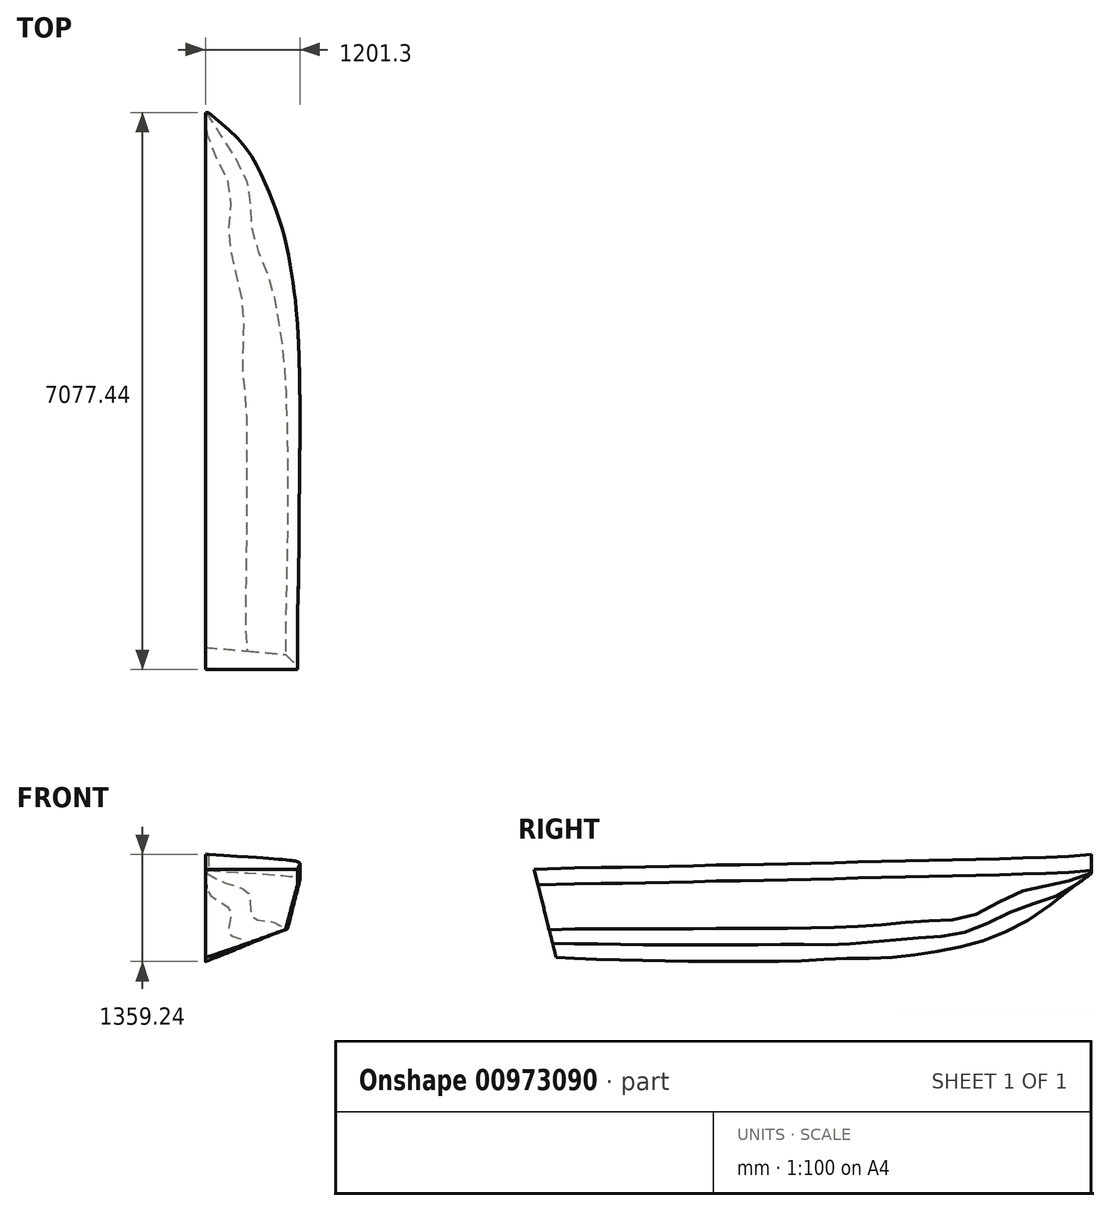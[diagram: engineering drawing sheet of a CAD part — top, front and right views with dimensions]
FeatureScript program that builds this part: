
annotation { "Feature Type Name" : "Feature", "Feature Type Description" : "" }
export const myFeature = defineFeature(function(context is Context, id is Id, definition is map)
    precondition{}
    {
        {
            var Q0;
            Q0=qCreatedBy(makeId("Front.planeOp"),FACE);
            cPlane(context, id + "F0", {"entities" : qUnion([Q0]), "cplaneType" : CPlaneType.OFFSET, "offset" : 946.15 * mm, "width" : 152.4 * mm, "height" : 152.4 * mm});
        }
        {
            var Q0;
            Q0=qCreatedBy(makeId("Front.planeOp"),FACE);
            cPlane(context, id + "F1", {"entities" : qUnion([Q0]), "cplaneType" : CPlaneType.OFFSET, "offset" : 1504.95 * mm, "width" : 152.4 * mm, "height" : 152.4 * mm});
        }
        {
            var Q0;
            Q0=qCreatedBy(id+"F0.planeOp",FACE);
            var sketch = newSketch(context, id + "F2", { "sketchPlane" : qUnion([Q0])});
            skFitSpline(sketch, "E0", {"points": [v(0, 457.2) * mm, v(304.8, 676.28) * mm], "startDerivative": vector(321.5, 180.35) * mm, "endDerivative": vector(258.3, 225.91) * mm});
            skFitSpline(sketch, "E1", {"points": [v(304.8, 676.28) * mm, v(781.05, 1120.78) * mm], "startDerivative": vector(578.23, 464.22) * mm, "endDerivative": vector(557.74, 597.41) * mm});
            skPoint(sketch, "E2.orphan", {"position": v(0, 1323.98) * mm});
            skLineSegment(sketch, "E3", {"start": v(781.05, 1120.78) * mm, "end": v(781.05, 1323.98) * mm});
            skLineSegment(sketch, "E4", {"start": v(781.05, 1323.98) * mm, "end": v(0, 1323.98) * mm});
            skLineSegment(sketch, "E5", {"start": v(0, 457.2) * mm, "end": v(0, 1323.98) * mm});
            skSolve(sketch);
        }
        {
            var Q0;
            Q0=qCreatedBy(id+"F1.planeOp",FACE);
            var sketch = newSketch(context, id + "F3", { "sketchPlane" : qUnion([Q0])});
            skLineSegment(sketch, "E6", {"start": v(0, 0) * mm, "end": v(0, 1308.1) * mm, "construction": true});
            skFitSpline(sketch, "E7", {"points": [v(0, 239.71) * mm, v(588.96, 593.73) * mm], "startDerivative": vector(594.9, 354.01) * mm, "endDerivative": vector(594.9, 354.01) * mm});
            skFitSpline(sketch, "E8", {"points": [v(981.07, 1104.9) * mm, v(588.96, 593.73) * mm], "startDerivative": vector(-386.18, -511.18) * mm, "endDerivative": vector(-386.18, -511.18) * mm});
            skLineSegment(sketch, "E9", {"start": v(0, 1308.1) * mm, "end": v(0, 239.71) * mm});
            skLineSegment(sketch, "E10", {"start": v(981.07, 1104.9) * mm, "end": v(981.07, 1308.1) * mm});
            skLineSegment(sketch, "E11", {"start": v(981.07, 1308.1) * mm, "end": v(0, 1308.1) * mm});
            skSolve(sketch);
        }
        {
            var Q0;
            Q0=qCreatedBy(makeId("Front.planeOp"),FACE);
            cPlane(context, id + "F4", {"entities" : qUnion([Q0]), "cplaneType" : CPlaneType.OFFSET, "offset" : 2063.75 * mm, "width" : 152.4 * mm, "height" : 152.4 * mm});
        }
        {
            var Q0;
            Q0=qCreatedBy(id+"F4.planeOp",FACE);
            var sketch = newSketch(context, id + "F5", { "sketchPlane" : qUnion([Q0])});
            skLineSegment(sketch, "E12", {"start": v(1232.35, 0) * mm, "end": v(0, 0) * mm, "construction": true});
            skLineSegment(sketch, "E13", {"start": v(0, 0) * mm, "end": v(0, 1357.14) * mm, "construction": true});
            skFitSpline(sketch, "E14", {"points": [v(0, 125.41) * mm, v(790.58, 527.05) * mm], "startDerivative": vector(784.32, 370.04) * mm, "endDerivative": vector(829.24, 425.02) * mm});
            skFitSpline(sketch, "E15", {"points": [v(1098.55, 1092.2) * mm, v(790.58, 527.05) * mm], "startDerivative": vector(-307.98, -565.15) * mm, "endDerivative": vector(-307.98, -565.15) * mm});
            skLineSegment(sketch, "E16", {"start": v(0, 1295.4) * mm, "end": v(0, 125.41) * mm});
            skLineSegment(sketch, "E17", {"start": v(1098.55, 1092.2) * mm, "end": v(1098.55, 1295.4) * mm});
            skLineSegment(sketch, "E18", {"start": v(1098.55, 1295.4) * mm, "end": v(0, 1295.4) * mm});
            skSolve(sketch);
        }
        {
            var Q0;
            Q0=qCreatedBy(makeId("Front.planeOp"),FACE);
            cPlane(context, id + "F6", {"entities" : qUnion([Q0]), "cplaneType" : CPlaneType.OFFSET, "offset" : 2622.55 * mm, "width" : 152.4 * mm, "height" : 152.4 * mm});
        }
        {
            var Q0;
            Q0=qCreatedBy(id+"F6.planeOp",FACE);
            var sketch = newSketch(context, id + "F7", { "sketchPlane" : qUnion([Q0])});
            skFitSpline(sketch, "E19", {"points": [v(0, 61.91) * mm, v(923.93, 483.74) * mm], "startDerivative": vector(732.65, 291.88) * mm, "endDerivative": vector(540.14, 261.57) * mm});
            skLineSegment(sketch, "E20", {"start": v(0, 0) * mm, "end": v(0, 1264.36) * mm, "construction": true});
            skLineSegment(sketch, "E21", {"start": v(0, 0) * mm, "end": v(1099.95, 0) * mm, "construction": true});
            skFitSpline(sketch, "E22", {"points": [v(923.93, 483.74) * mm, v(1163.64, 1079.5) * mm], "startDerivative": vector(239.71, 595.76) * mm, "endDerivative": vector(239.71, 595.76) * mm});
            skLineSegment(sketch, "E23", {"start": v(0, 1282.7) * mm, "end": v(0, 61.91) * mm});
            skLineSegment(sketch, "E24", {"start": v(1163.64, 1079.5) * mm, "end": v(1163.64, 1282.7) * mm});
            skLineSegment(sketch, "E25", {"start": v(1163.64, 1282.7) * mm, "end": v(0, 1282.7) * mm});
            skSolve(sketch);
        }
        {
            var Q0;
            Q0=qCreatedBy(makeId("Front.planeOp"),FACE);
            cPlane(context, id + "F8", {"entities" : qUnion([Q0]), "cplaneType" : CPlaneType.OFFSET, "offset" : 3181.35 * mm, "width" : 152.4 * mm, "height" : 152.4 * mm});
        }
        {
            var Q0;
            Q0=qCreatedBy(id+"F8.planeOp",FACE);
            var sketch = newSketch(context, id + "F9", { "sketchPlane" : qUnion([Q0])});
            skLineSegment(sketch, "E26", {"start": v(0, 0) * mm, "end": v(0, 1556.52) * mm, "construction": true});
            skLineSegment(sketch, "E27", {"start": v(0, 0) * mm, "end": v(1752.69, 0) * mm, "construction": true});
            skFitSpline(sketch, "E28", {"points": [v(1190.62, 1066.8) * mm, v(996.95, 450.85) * mm], "startDerivative": vector(-132.19, -462.86) * mm, "endDerivative": vector(-164.13, -469.98) * mm});
            skFitSpline(sketch, "E29", {"points": [v(0, 47.63) * mm, v(996.95, 450.85) * mm], "startDerivative": vector(841.43, 311.9) * mm, "endDerivative": vector(1084.4, 465.95) * mm});
            skLineSegment(sketch, "E30", {"start": v(0, 1270) * mm, "end": v(0, 47.63) * mm});
            skLineSegment(sketch, "E31", {"start": v(1190.62, 1066.8) * mm, "end": v(1190.62, 1270) * mm});
            skLineSegment(sketch, "E32", {"start": v(1190.62, 1270) * mm, "end": v(0, 1270) * mm});
            skSolve(sketch);
        }
        {
            var Q0;
            Q0=qCreatedBy(makeId("Front.planeOp"),FACE);
            cPlane(context, id + "F10", {"entities" : qUnion([Q0]), "cplaneType" : CPlaneType.OFFSET, "offset" : 3740.15 * mm, "width" : 152.4 * mm, "height" : 152.4 * mm});
        }
        {
            var Q0;
            Q0=qCreatedBy(makeId("Front.planeOp"),FACE);
            cPlane(context, id + "F11", {"entities" : qUnion([Q0]), "cplaneType" : CPlaneType.OFFSET, "offset" : 4298.95 * mm, "width" : 152.4 * mm, "height" : 152.4 * mm});
        }
        {
            var Q0;
            Q0=qCreatedBy(makeId("Front.planeOp"),FACE);
            cPlane(context, id + "F12", {"entities" : qUnion([Q0]), "cplaneType" : CPlaneType.OFFSET, "offset" : 4857.75 * mm, "width" : 152.4 * mm, "height" : 152.4 * mm});
        }
        {
            var Q0;
            Q0=qCreatedBy(id+"F10.planeOp",FACE);
            var sketch = newSketch(context, id + "F13", { "sketchPlane" : qUnion([Q0])});
            skFitSpline(sketch, "E33", {"points": [v(0, 19.05) * mm, v(1028.7, 438.15) * mm], "startDerivative": vector(970.18, 370.37) * mm, "endDerivative": vector(970.18, 370.37) * mm});
            skFitSpline(sketch, "E34", {"points": [v(1028.7, 438.15) * mm, v(1200.15, 1054.1) * mm], "startDerivative": vector(218.26, 648.15) * mm, "endDerivative": vector(218.26, 648.15) * mm});
            skLineSegment(sketch, "E35", {"start": v(0, 1257.3) * mm, "end": v(0, 19.05) * mm});
            skLineSegment(sketch, "E36", {"start": v(1200.15, 1054.1) * mm, "end": v(1200.15, 1257.3) * mm});
            skLineSegment(sketch, "E37", {"start": v(1200.15, 1257.3) * mm, "end": v(0, 1257.3) * mm});
            skSolve(sketch);
        }
        {
            var Q0;
            Q0=qCreatedBy(id+"F11.planeOp",FACE);
            var sketch = newSketch(context, id + "F14", { "sketchPlane" : qUnion([Q0])});
            skFitSpline(sketch, "E38", {"points": [v(0, 12.7) * mm, v(1041.4, 431.8) * mm], "startDerivative": vector(1043.47, 392.9) * mm, "endDerivative": vector(1043.47, 392.9) * mm});
            skFitSpline(sketch, "E39", {"points": [v(1041.4, 431.8) * mm, v(1198.56, 1041.4) * mm], "startDerivative": vector(159.83, 619.33) * mm, "endDerivative": vector(159.83, 619.33) * mm});
            skLineSegment(sketch, "E40", {"start": v(0, 1244.6) * mm, "end": v(0, 12.7) * mm});
            skLineSegment(sketch, "E41", {"start": v(1198.56, 1041.4) * mm, "end": v(1198.56, 1244.6) * mm});
            skLineSegment(sketch, "E42", {"start": v(1198.56, 1244.6) * mm, "end": v(0, 1244.6) * mm});
            skSolve(sketch);
        }
        {
            var Q0;
            Q0=qCreatedBy(id+"F12.planeOp",FACE);
            var sketch = newSketch(context, id + "F15", { "sketchPlane" : qUnion([Q0])});
            skFitSpline(sketch, "E43", {"points": [v(0, 12.7) * mm, v(1041.4, 430.21) * mm], "startDerivative": vector(442.9, 153.73) * mm, "endDerivative": vector(442.9, 153.73) * mm});
            skFitSpline(sketch, "E44", {"points": [v(1041.4, 430.21) * mm, v(1192.21, 1031.88) * mm], "startDerivative": vector(84.12, 287.16) * mm, "endDerivative": vector(84.12, 287.16) * mm});
            skLineSegment(sketch, "E45", {"start": v(0, 1235.07) * mm, "end": v(0, 12.7) * mm});
            skLineSegment(sketch, "E46", {"start": v(1192.21, 1031.88) * mm, "end": v(1192.21, 1235.08) * mm});
            skLineSegment(sketch, "E47", {"start": v(1192.21, 1235.08) * mm, "end": v(0, 1235.08) * mm});
            skSolve(sketch);
        }
        {
            var Q0;
            Q0=qCreatedBy(makeId("Front.planeOp"),FACE);
            cPlane(context, id + "F16", {"entities" : qUnion([Q0]), "cplaneType" : CPlaneType.OFFSET, "offset" : 5416.55 * mm, "width" : 152.4 * mm, "height" : 152.4 * mm});
        }
        {
            var Q0;
            Q0=qCreatedBy(makeId("Front.planeOp"),FACE);
            cPlane(context, id + "F17", {"entities" : qUnion([Q0]), "cplaneType" : CPlaneType.OFFSET, "offset" : 5975.35 * mm, "width" : 152.4 * mm, "height" : 152.4 * mm});
        }
        {
            var Q0;
            Q0=qCreatedBy(makeId("Front.planeOp"),FACE);
            cPlane(context, id + "F18", {"entities" : qUnion([Q0]), "cplaneType" : CPlaneType.OFFSET, "offset" : 6534.15 * mm, "width" : 152.4 * mm, "height" : 152.4 * mm});
        }
        {
            var Q0;
            Q0=qCreatedBy(makeId("Front.planeOp"),FACE);
            var sketch = newSketch(context, id + "F19", { "sketchPlane" : qUnion([Q0])});
            skFitSpline(sketch, "E48", {"points": [v(0, 1016) * mm, v(0, 1130.3) * mm], "startDerivative": vector(0, 222.3) * mm, "endDerivative": vector(0, 222.3) * mm});
            skFitSpline(sketch, "E49", {"points": [v(0, 1130.3) * mm, v(25.4, 1143) * mm], "startDerivative": vector(102.32, 168.4) * mm, "endDerivative": vector(102.32, 168.4) * mm});
            skSolve(sketch);
        }
        {
            var Q0;
            Q0=qCreatedBy(makeId("Front.planeOp"),FACE);
            cPlane(context, id + "F20", {"entities" : qUnion([Q0]), "cplaneType" : CPlaneType.OFFSET, "offset" : 6781.8 * mm, "width" : 152.4 * mm, "height" : 152.4 * mm});
        }
        {
            var Q0;
            Q0=qCreatedBy(id+"F20.planeOp",FACE);
            var sketch = newSketch(context, id + "F21", { "sketchPlane" : qUnion([Q0])});
            skLineSegment(sketch, "E50", {"start": v(-392.79, 0) * mm, "end": v(597.43, 0) * mm, "construction": true});
            skSolve(sketch);
        }
        {
            var Q0;
            Q0=sQuery(id+"F21.wireOp",EDGE,"E50");
            cPlane(context, id + "F22", {"entities" : qUnion([Q0]), "cplaneType" : CPlaneType.LINE_ANGLE, "offset" : 25.4 * mm, "angle" : 14 * degree, "width" : 152.4 * mm, "height" : 152.4 * mm});
        }
        {
            var Q0;
            Q0=qCreatedBy(id+"F16.planeOp",FACE);
            var sketch = newSketch(context, id + "F23", { "sketchPlane" : qUnion([Q0])});
            skFitSpline(sketch, "E51", {"points": [v(0, 19.05) * mm, v(1039.81, 425.45) * mm], "startDerivative": vector(1108.96, 386.68) * mm, "endDerivative": vector(1108.96, 386.68) * mm});
            skFitSpline(sketch, "E52", {"points": [v(1039.81, 425.45) * mm, v(1187.45, 1017.59) * mm], "startDerivative": vector(186.18, 680.26) * mm, "endDerivative": vector(186.18, 680.26) * mm});
            skLineSegment(sketch, "E53", {"start": v(0, 1220.79) * mm, "end": v(0, 19.05) * mm});
            skLineSegment(sketch, "E54", {"start": v(1187.45, 1017.59) * mm, "end": v(1187.45, 1220.79) * mm});
            skLineSegment(sketch, "E55", {"start": v(1187.45, 1220.79) * mm, "end": v(0, 1220.79) * mm});
            skSolve(sketch);
        }
        {
            var Q0;
            Q0=qCreatedBy(id+"F17.planeOp",FACE);
            var sketch = newSketch(context, id + "F24", { "sketchPlane" : qUnion([Q0])});
            skFitSpline(sketch, "E56", {"points": [v(0, 31.75) * mm, v(1028.7, 425.45) * mm], "startDerivative": vector(1097.64, 394.36) * mm, "endDerivative": vector(1097.64, 394.36) * mm});
            skFitSpline(sketch, "E57", {"points": [v(1028.7, 425.45) * mm, v(1181.1, 1006.48) * mm], "startDerivative": vector(169.01, 647.88) * mm, "endDerivative": vector(169.01, 647.88) * mm});
            skLineSegment(sketch, "E58", {"start": v(0, 1209.67) * mm, "end": v(0, 31.75) * mm});
            skLineSegment(sketch, "E59", {"start": v(1181.1, 1006.48) * mm, "end": v(1181.1, 1209.67) * mm});
            skLineSegment(sketch, "E60", {"start": v(1181.1, 1209.67) * mm, "end": v(0, 1209.67) * mm});
            skSolve(sketch);
        }
        {
            var Q0;
            Q0=qCreatedBy(id+"F18.planeOp",FACE);
            var sketch = newSketch(context, id + "F25", { "sketchPlane" : qUnion([Q0])});
            skFitSpline(sketch, "E61", {"points": [v(0, 50.8) * mm, v(1017.59, 425.45) * mm], "startDerivative": vector(1094.64, 393.84) * mm, "endDerivative": vector(1094.64, 393.84) * mm});
            skFitSpline(sketch, "E62", {"points": [v(1017.59, 425.45) * mm, v(1168.4, 996.95) * mm], "startDerivative": vector(200.5, 665.94) * mm, "endDerivative": vector(200.5, 665.94) * mm});
            skLineSegment(sketch, "E63", {"start": v(0, 1200.15) * mm, "end": v(0, 50.8) * mm});
            skLineSegment(sketch, "E64", {"start": v(1168.4, 996.95) * mm, "end": v(1168.4, 1200.15) * mm});
            skLineSegment(sketch, "E65", {"start": v(1168.4, 1200.15) * mm, "end": v(0, 1200.15) * mm});
            skSolve(sketch);
        }
        {
            var Q0;
            Q0=qCreatedBy(makeId("Right.planeOp"),FACE);
            var sketch = newSketch(context, id + "F26", { "sketchPlane" : qUnion([Q0])});
            skFitSpline(sketch, "E66", {"points": [v(-6534.15, 1200.15) * mm, v(-7077.44, 1185.75) * mm], "startDerivative": vector(-630.16, -14) * mm, "endDerivative": vector(-630.16, -14) * mm});
            skLineSegment(sketch, "E67", {"start": v(-6746.73, -140.66) * mm, "end": v(-7111.62, 1322.83) * mm});
            skSolve(sketch);
        }
        {
            var Q0;
            Q0=qCreatedBy(id+"F22.planeOp",FACE);
            var sketch = newSketch(context, id + "F27", { "sketchPlane" : qUnion([Q0])});
            skFitSpline(sketch, "E68", {"points": [v(0, 1705.8) * mm, v(-1016.02, 2070.9) * mm], "startDerivative": vector(-1148.3, 369.29) * mm, "endDerivative": vector(-981.9, 351.99) * mm});
            skFitSpline(sketch, "E69", {"points": [v(-1016.02, 2070.9) * mm, v(-1173.94, 2677.54) * mm], "startDerivative": vector(-176, 689.29) * mm, "endDerivative": vector(-179.1, 688.48) * mm});
            skLineSegment(sketch, "E70", {"start": v(-1169.05, 2658.74) * mm, "end": v(-1169.05, 2862.72) * mm});
            skLineSegment(sketch, "E71", {"start": v(-1169.05, 2862.72) * mm, "end": v(0, 2862.72) * mm});
            skLineSegment(sketch, "E72", {"start": v(0, 2862.72) * mm, "end": v(0, 1705.8) * mm});
            skSolve(sketch);
        }
        {
            var Q0;
            Q0=qCreatedBy(makeId("Top.planeOp"),FACE);
            var sketch = newSketch(context, id + "F28", { "sketchPlane" : qUnion([Q0])});
            skFitSpline(sketch, "E73", {"points": [v(0, 0) * mm, v(431.8, -355.25) * mm, v(781.05, -946.15) * mm], "startDerivative": vector(1155.65, -733.6) * mm, "endDerivative": vector(458.6, -1130.27) * mm});
            skLineSegment(sketch, "E74", {"start": v(431.8, -355.25) * mm, "end": v(1147.17, -355.25) * mm, "construction": true});
            skLineSegment(sketch, "E75", {"start": v(431.8, -355.25) * mm, "end": v(431.8, 130.5) * mm, "construction": true});
            skSolve(sketch);
        }
        {
            var Q0;
            Q0=sQuery(id+"F28.wireOp",EDGE,"E74");
            cPlane(context, id + "F29", {"entities" : qUnion([Q0]), "cplaneType" : CPlaneType.LINE_ANGLE, "offset" : 25.4 * mm, "angle" : 0 * degree, "width" : 152.4 * mm, "height" : 152.4 * mm});
        }
        {
            var Q0;
            Q0=qCreatedBy(makeId("Right.planeOp"),FACE);
            var sketch = newSketch(context, id + "F30", { "sketchPlane" : qUnion([Q0])});
            skLineSegment(sketch, "E76", {"start": v(0, 0) * mm, "end": v(0, 1689.84) * mm, "construction": true});
            skFitSpline(sketch, "E77", {"points": [v(-946.15, 1120.78) * mm, v(-355.25, 1142.63) * mm, v(0, 1146.17) * mm], "startDerivative": vector(1027.65, 28.5) * mm, "endDerivative": vector(950.59, 8.16) * mm});
            skFitSpline(sketch, "E78", {"points": [v(-946.15, 676.28) * mm, v(-355.25, 859.78) * mm, v(0, 1146.17) * mm], "startDerivative": vector(1207.8, 162.55) * mm, "endDerivative": vector(906.92, 873.18) * mm});
            skFitSpline(sketch, "E79", {"points": [v(-946.15, 457.2) * mm, v(-355.25, 859.78) * mm], "startDerivative": vector(690.66, 418.33) * mm, "endDerivative": vector(524.17, 381.36) * mm});
            skFitSpline(sketch, "E80", {"points": [v(-2063.75, 1092.2) * mm, v(-1504.95, 1104.9) * mm, v(-946.15, 1120.78) * mm, v(139.14, 1151.53) * mm], "startDerivative": vector(1935.44, 15.71) * mm, "endDerivative": vector(2871.35, 117.85) * mm, "construction": true});
            skLineSegment(sketch, "E81", {"start": v(-355.25, 71.74) * mm, "end": v(-355.25, 1647.82) * mm, "construction": true});
            skPoint(sketch, "E82", {"position": v(-238.1, 933.93) * mm});
            skSolve(sketch);
        }
        {
            var Q0;
            Q0=qCreatedBy(id+"F29.planeOp",FACE);
            var sketch = newSketch(context, id + "F31", { "sketchPlane" : qUnion([Q0])});
            skLineSegment(sketch, "E83", {"start": v(-431.8, 0) * mm, "end": v(-431.8, 1295.57) * mm, "construction": true});
            skLineSegment(sketch, "E84", {"start": v(0, 1142.63) * mm, "end": v(-1416.64, 1142.63) * mm, "construction": true});
            skLineSegment(sketch, "E85", {"start": v(0, 859.78) * mm, "end": v(-770.97, 859.78) * mm, "construction": true});
            skLineSegment(sketch, "E86", {"start": v(-431.8, 1142.63) * mm, "end": v(-431.8, 1345.83) * mm});
            skLineSegment(sketch, "E87", {"start": v(-431.8, 1345.83) * mm, "end": v(0, 1345.83) * mm});
            skLineSegment(sketch, "E88", {"start": v(0, 1345.83) * mm, "end": v(0, 859.78) * mm});
            skLineSegment(sketch, "E89", {"start": v(-431.8, 1142.63) * mm, "end": v(-39.04, 888.57) * mm});
            skFitSpline(sketch, "E90", {"points": [v(-39.04, 888.57) * mm, v(0, 859.78) * mm], "startDerivative": vector(71.38, -49.03) * mm, "endDerivative": vector(74.53, -65.76) * mm});
            skSolve(sketch);
        }
        {
            var Q0;
            Q0=qCreatedBy(makeId("Front.planeOp"),FACE);
            var sketch = newSketch(context, id + "F32", { "sketchPlane" : qUnion([Q0])});
            skLineSegment(sketch, "E91", {"start": v(0, 1371.6) * mm, "end": v(0, 1168.4) * mm});
            skLineSegment(sketch, "E92", {"start": v(0, 1371.6) * mm, "end": v(36.91, 1371.6) * mm});
            skLineSegment(sketch, "E93", {"start": v(36.91, 1371.6) * mm, "end": v(36.91, 1168.4) * mm});
            skLineSegment(sketch, "E94", {"start": v(0, 1130.3) * mm, "end": v(0, 1168.4) * mm});
            skFitSpline(sketch, "E95", {"points": [v(36.91, 1168.4) * mm, v(10.97, 1137.92) * mm], "startDerivative": vector(-19.12, -24.4) * mm, "endDerivative": vector(-29.72, -30.1) * mm});
            skFitSpline(sketch, "E96", {"points": [v(10.97, 1137.92) * mm, v(0, 1130.3) * mm], "startDerivative": vector(-8.94, -7.74) * mm, "endDerivative": vector(-12.05, -8.93) * mm});
            skSolve(sketch);
        }
        {
            var Q0;
            Q0 = qSketchRegion(id + "F32", true);
            var Q1;
            Q1 = qSketchRegion(id + "F31", true);
            var Q2;
            Q2 = qSketchRegion(id + "F2", true);
            var Q3;
            Q3 = qSketchRegion(id + "F3", true);
            var Q4;
            Q4 = qSketchRegion(id + "F5", true);
            var Q5;
            Q5 = qSketchRegion(id + "F7", true);
            var Q6;
            Q6 = qSketchRegion(id + "F9", true);
            var Q7;
            Q7 = qSketchRegion(id + "F13", true);
            var Q8;
            Q8 = qSketchRegion(id + "F14", true);
            var Q9;
            Q9 = qSketchRegion(id + "F15", true);
            var Q10;
            Q10 = qSketchRegion(id + "F23", true);
            var Q11;
            Q11 = qSketchRegion(id + "F24", true);
            var Q12;
            Q12 = qSketchRegion(id + "F25", true);
            var Q13;
            Q13 = qSketchRegion(id + "F27", true);
            loft(context, id + "F33", {"sheetProfilesArray" : [{ "sheetProfileEntities" : qUnion([Q0]) }, { "sheetProfileEntities" : qUnion([Q1]) }, { "sheetProfileEntities" : qUnion([Q2]) }, { "sheetProfileEntities" : qUnion([Q3]) }, { "sheetProfileEntities" : qUnion([Q4]) }, { "sheetProfileEntities" : qUnion([Q5]) }, { "sheetProfileEntities" : qUnion([Q6]) }, { "sheetProfileEntities" : qUnion([Q7]) }, { "sheetProfileEntities" : qUnion([Q8]) }, { "sheetProfileEntities" : qUnion([Q9]) }, { "sheetProfileEntities" : qUnion([Q10]) }, { "sheetProfileEntities" : qUnion([Q11]) }, { "sheetProfileEntities" : qUnion([Q12]) }, { "sheetProfileEntities" : qUnion([Q13]) }]});
        }
    });
